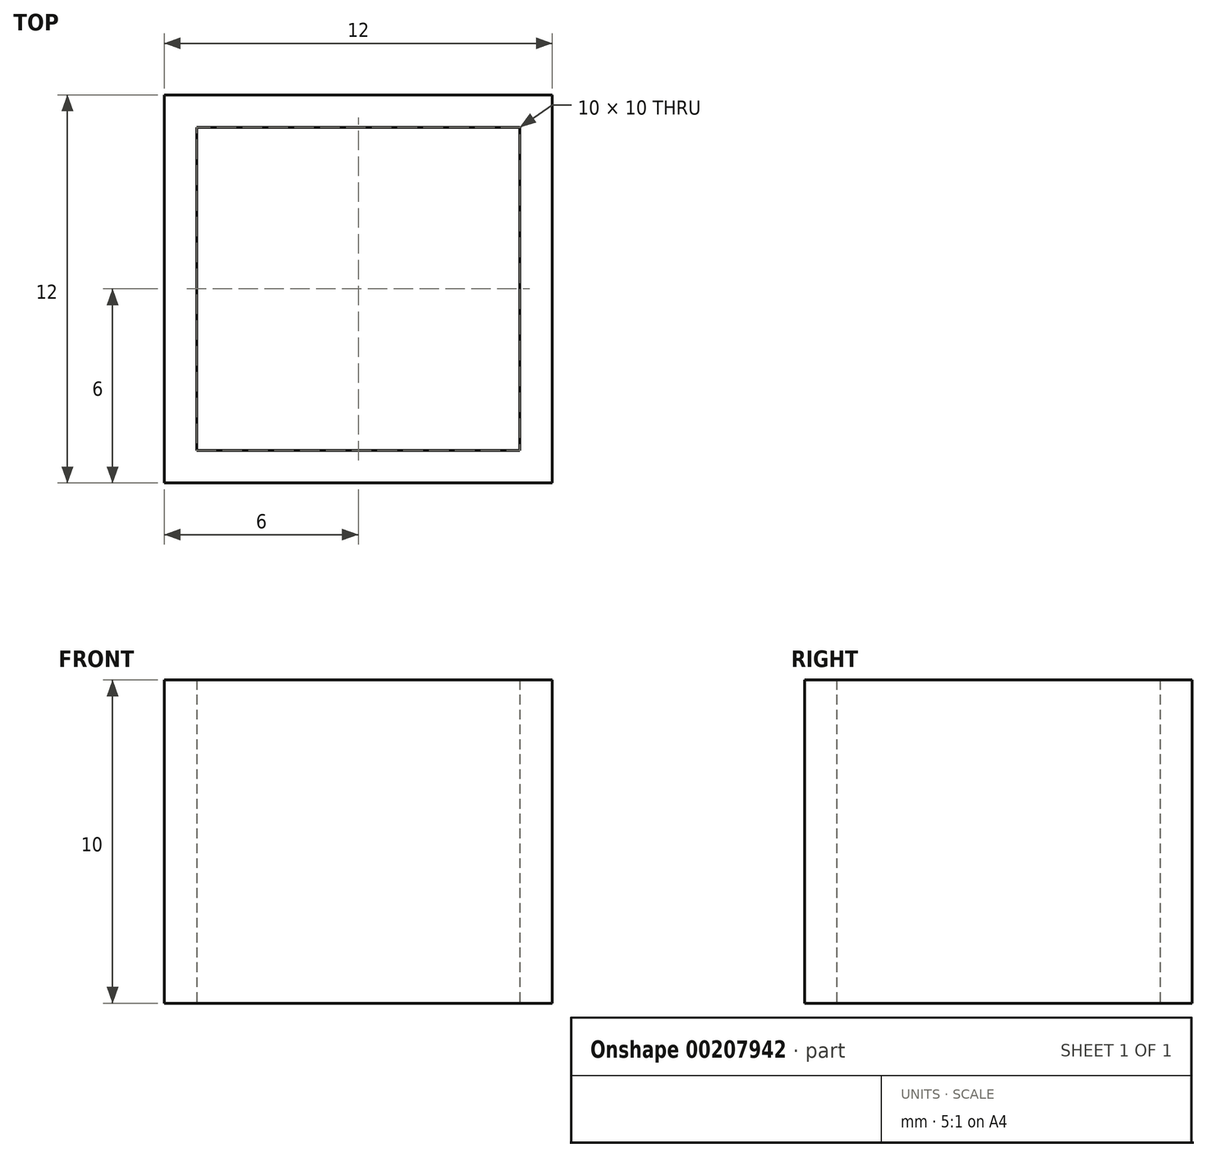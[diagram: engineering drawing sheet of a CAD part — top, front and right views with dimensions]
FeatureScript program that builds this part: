
annotation { "Feature Type Name" : "Feature", "Feature Type Description" : "" }
export const myFeature = defineFeature(function(context is Context, id is Id, definition is map)
    precondition{}
    {
        {
            var Q0;
            Q0=qCreatedBy(makeId("Top.planeOp"),FACE);
            var sketch = newSketch(context, id + "F0", { "sketchPlane" : qUnion([Q0])});
            skLineSegment(sketch, "E0.bottom", {"start": v(5, 5) * mm, "end": v(-5, 5) * mm});
            skLineSegment(sketch, "E0.top", {"start": v(5, -5) * mm, "end": v(-5, -5) * mm});
            skLineSegment(sketch, "E0.left", {"start": v(5, 5) * mm, "end": v(5, -5) * mm});
            skLineSegment(sketch, "E0.right", {"start": v(-5, 5) * mm, "end": v(-5, -5) * mm});
            skPoint(sketch, "E0.middle", {"position": v(0, 0) * mm});
            skLineSegment(sketch, "E1.0", {"start": v(6, 6) * mm, "end": v(-6, 6) * mm});
            skLineSegment(sketch, "E1.1", {"start": v(6, 6) * mm, "end": v(6, -6) * mm});
            skLineSegment(sketch, "E1.2", {"start": v(6, -6) * mm, "end": v(-6, -6) * mm});
            skLineSegment(sketch, "E1.3", {"start": v(-6, 6) * mm, "end": v(-6, -6) * mm});
            skSolve(sketch);
        }
        {
            var Q0;
            Q0=makeQuery(id+"F0.imprint","IMPRINT",FACE,{"disambiguationData":[TD([[makeQuery(id+"F0.imprint","IMPRINT",EDGE,{"derivedFrom":sQuery(id+"F0.wireOp",EDGE,"E0.bottom")}),-1.0]])]});
            extrude(context, id + "F1", {"entities" : qUnion([Q0]), "depth" : 10 * mm});
        }
    });
